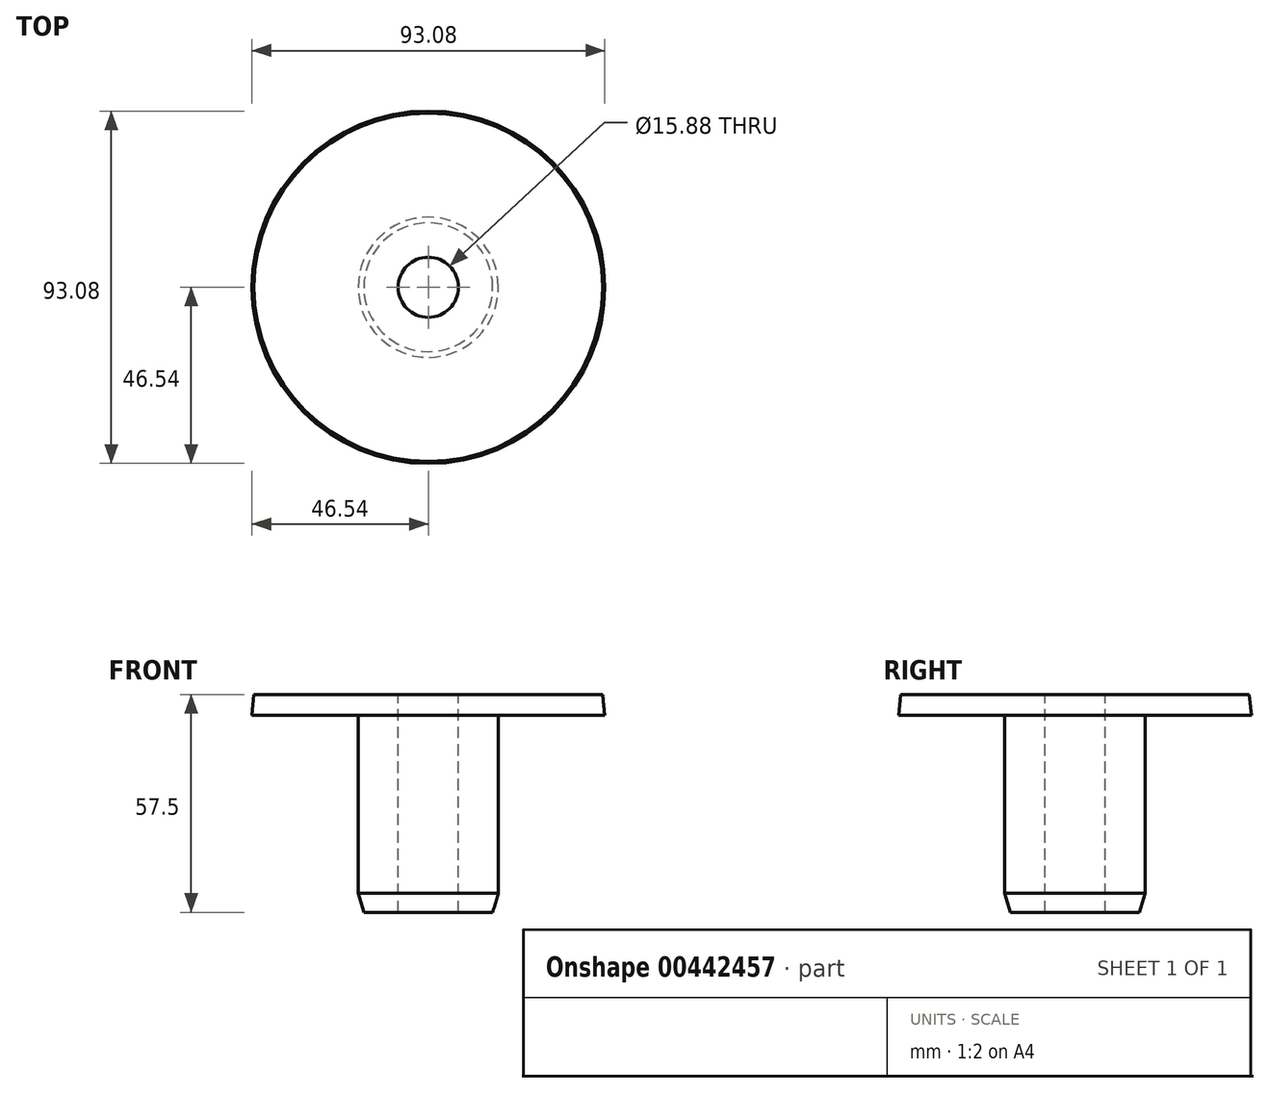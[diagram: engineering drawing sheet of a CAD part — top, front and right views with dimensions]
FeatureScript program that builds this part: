
annotation { "Feature Type Name" : "Feature", "Feature Type Description" : "" }
export const myFeature = defineFeature(function(context is Context, id is Id, definition is map)
    precondition{}
    {
        {
            var Q0;
            Q0=qCreatedBy(makeId("Top.planeOp"),FACE);
            var sketch = newSketch(context, id + "F0", { "sketchPlane" : qUnion([Q0])});
            skCircle(sketch, "E0", {"center": v(0, 0) * mm, "radius": 18.5 * mm});
            skSolve(sketch);
        }
        {
            var Q0;
            Q0 = qSketchRegion(id + "F0", true);
            extrude(context, id + "F1", {"entities" : qUnion([Q0]), "depth" : 52 * mm});
        }
        {
            var Q0;
            Q0=makeQuery(id+"F1.opExtrude","CAP_EDGE",EDGE,{"disambiguationData":[OSD([sQuery(id+"F0.wireOp",EDGE,"E0")])],"isStart":true});
            chamfer(context, id + "F2", {"entities" : qUnion([Q0]), "chamferType" : ChamferType.TWO_OFFSETS, "width1" : 5 * mm, "oppositeDirection" : false, "width2" : 1.5 * mm, "tangentPropagation" : true});
        }
        {
            var Q0;
            Q0=makeQuery(id+"F1.opExtrude","CAP_FACE",FACE,{"disambiguationData":[OSD([sQuery(id+"F0.wireOp",EDGE,"E0")])],"isStart":false});
            var sketch = newSketch(context, id + "F3", { "sketchPlane" : qUnion([Q0])});
            skCircle(sketch, "E1", {"center": v(0, 0) * mm, "radius": 47 * mm});
            skSolve(sketch);
        }
        {
            var Q0;
            Q0 = qSketchRegion(id + "F3", true);
            extrude(context, id + "F4", {"entities" : qUnion([Q0]), "operationType" : NewBodyOperationType.ADD, "depth" : 5.5 * mm});
        }
        {
            var Q0;
            Q0=makeQuery(id+"F4.opExtrude","CAP_EDGE",EDGE,{"disambiguationData":[OSD([sQuery(id+"F3.wireOp",EDGE,"E1")])],"isStart":false});
            chamfer(context, id + "F5", {"entities" : qUnion([Q0]), "chamferType" : ChamferType.TWO_OFFSETS, "width1" : 1 * mm, "oppositeDirection" : false, "width2" : 10.2 * mm, "tangentPropagation" : true});
        }
        {
            var Q0;
            Q0=makeQuery(id+"F4.opExtrude","CAP_FACE",FACE,{"disambiguationData":[OSD([sQuery(id+"F3.wireOp",EDGE,"E1")])],"isStart":false});
            var sketch = newSketch(context, id + "F6", { "sketchPlane" : qUnion([Q0])});
            skCircle(sketch, "E2", {"center": v(0, 0) * mm, "radius": 7.94 * mm});
            skSolve(sketch);
        }
        {
            var Q0;
            Q0 = qSketchRegion(id + "F6", true);
            extrude(context, id + "F7", {"entities" : qUnion([Q0]), "operationType" : NewBodyOperationType.REMOVE, "endBound" : BoundingType.THROUGH_ALL, "oppositeDirection" : true, "depth" : 25 * mm});
        }
    });
